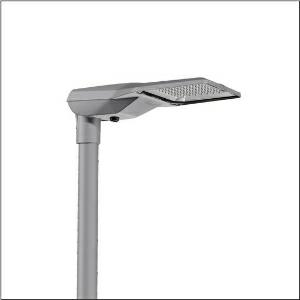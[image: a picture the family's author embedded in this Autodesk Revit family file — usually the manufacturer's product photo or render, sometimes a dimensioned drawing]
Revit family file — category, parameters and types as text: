
# Revit family: streetlight_sl_21_midi___st1_0a_5xe3d33r08mb_0fe4
name_source: partatom
category: Lighting Fixtures
units: mm (PartAtom-declared; Revit-internal decimal feet)

## family parameters
Cut with Voids When Loaded = No
Host = Face
Light Source = No
Part Type = Normal
Room Calculation Point = No
Round Connector Dimension = Use Diameter
Shared = No

## types (1)
- --- (1 x LED, 18270 lm, 136 W, 3000K)
    Apparent Load = 136 VA
    CIE Flux Codes = 37 72 97 100 100
    Color Rendering = 70
    Color Temperature = 3000K
    Default Elevation = 1800 mm
    Description = Streetlight SL 21 midi, mast luminaire, primary light control with lens, of PMMA, primary optical cover: cover, of toughened safety glass, transparent, light distribution: ST1.0a, light emission: direct distribution, primary light characteristic: asymmetric, installation type: side-entry, post-top, LED, High Power LED, rated luminous flux: 18.270lm, luminous efficacy: 134lm/W, light colour: 730, colour temperature: 3000K, control gear: D4i, control: flexible luminous flux parameterisation, time-dependent luminous flux control, constant luminous flux control, overheat protection, pre-setting: logarithmic dimming characteristic, mains connection: 230..240V, AC, 50/60Hz, start of lifetime: 136W, end of service life: 142W, reduction: 61W, luminaire housing, of diecast aluminium, powder-coated, SITECO metallic grey (DB 702S), corrosivity category C5 high according to DIN EN ISO 12944, please order mast flange separately, inclination adjustable: 0°, 5°, 10°, 15°, sealing non-destructively replaceable, multi-level sealing system, length: 644mm, width: 335mm, height: 110mm, mast flange for spigot size: 42mm (side-entry): 5XC10008XM4, 60/48mm (side-entry/post-top): 5XC10108XM2, 76/60mm (side-entry/post-top): 5XC10108XM1, mounting height: 4..8m, Smart Interface below, protection rating (complete): IP66, insulation class (complete): insulation class II (safety insulation), certification: CE, ENEC, ENEC+, VDE, impact resistance: IK10, permissible operating ambient temperature for outdoor applications: -40..+50°C, standard-compliant lighting for roads and squares, packaging unit: 1 piece

Light Distribution: ST1.0a
    Height = 111 mm
    Lamp = 1 x LED
    Lamp Light Flux = 18270 lm
    Lamp Power = 136 W
    Lamp count = 1
    Length = 644 mm
    Luminous efficacy = 134 lm/W
    Manufacturer = Siteco
    ModVariant = No
    Model = 5XE3D33R08MB
    Number of Poles = 1
    OnlyDefault = Yes
    Power Factor = 1
    Product Name = Streetlight SL 21 midi | ST1.0a
    Product group = mast luminaire | pylon top
    ProductGroupID = 6100
    Protection Class = Protection class II
    Protection Degree = IP 66
    RLX_Detail_Level = 1
    RLX_Emergency_Light_Flux = 0 lm
    RLX_Emergency_Type = 0
    RLX_Emergency_Type_DB = No
    RlxData = <blob elided: 26973 chars, md5=ec13b1a9>
    Socket = socket
    Standby Power = 0 W
    System Light Flux = 18270 lm
    System Power = 136 W
    Type Comments = factory setting: luminous flux: 100 % | dim-lin: 254 | 695 mA
    Type Image = l_1004300.jpg
    URL = http://relux.com
    VarID = @adj_186845
    Voltage = 0 V
    Weight = 0.00 kg
    Width = 336 mm

## geometry (parser evidence)
native form markers: Blend x4, Sweep x10
no freeform markers — native parametric forms only
